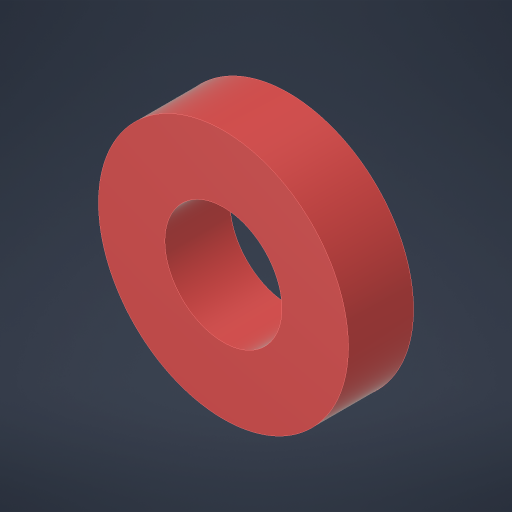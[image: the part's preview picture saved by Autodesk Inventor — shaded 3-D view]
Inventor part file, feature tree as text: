
AUTODESK INVENTOR PART (.ipt)
format: ipt  version: 2023.4 (Build 274418000, 418)  size: 172,032 bytes
history: native  units: in
note: dims shown in document units (in); Inventor stores cm internally (conversion verified against a paired STEP export)
features: extrude x1, sketch x1
ambient origin geometry x8: Origin, YZ Plane, XZ Plane, XY Plane, X Axis, Y Axis, Z Axis, Center Point
bodies: Solid1 (feature_tree)
feature tree (2):
  extrude  "Extrusion1"  Depth=0.49in TaperAngle=0.0deg
  sketch  "Sketch1"  dims[d0=0.5in d1=0.49in d2=0.0in d3=0.88in]
